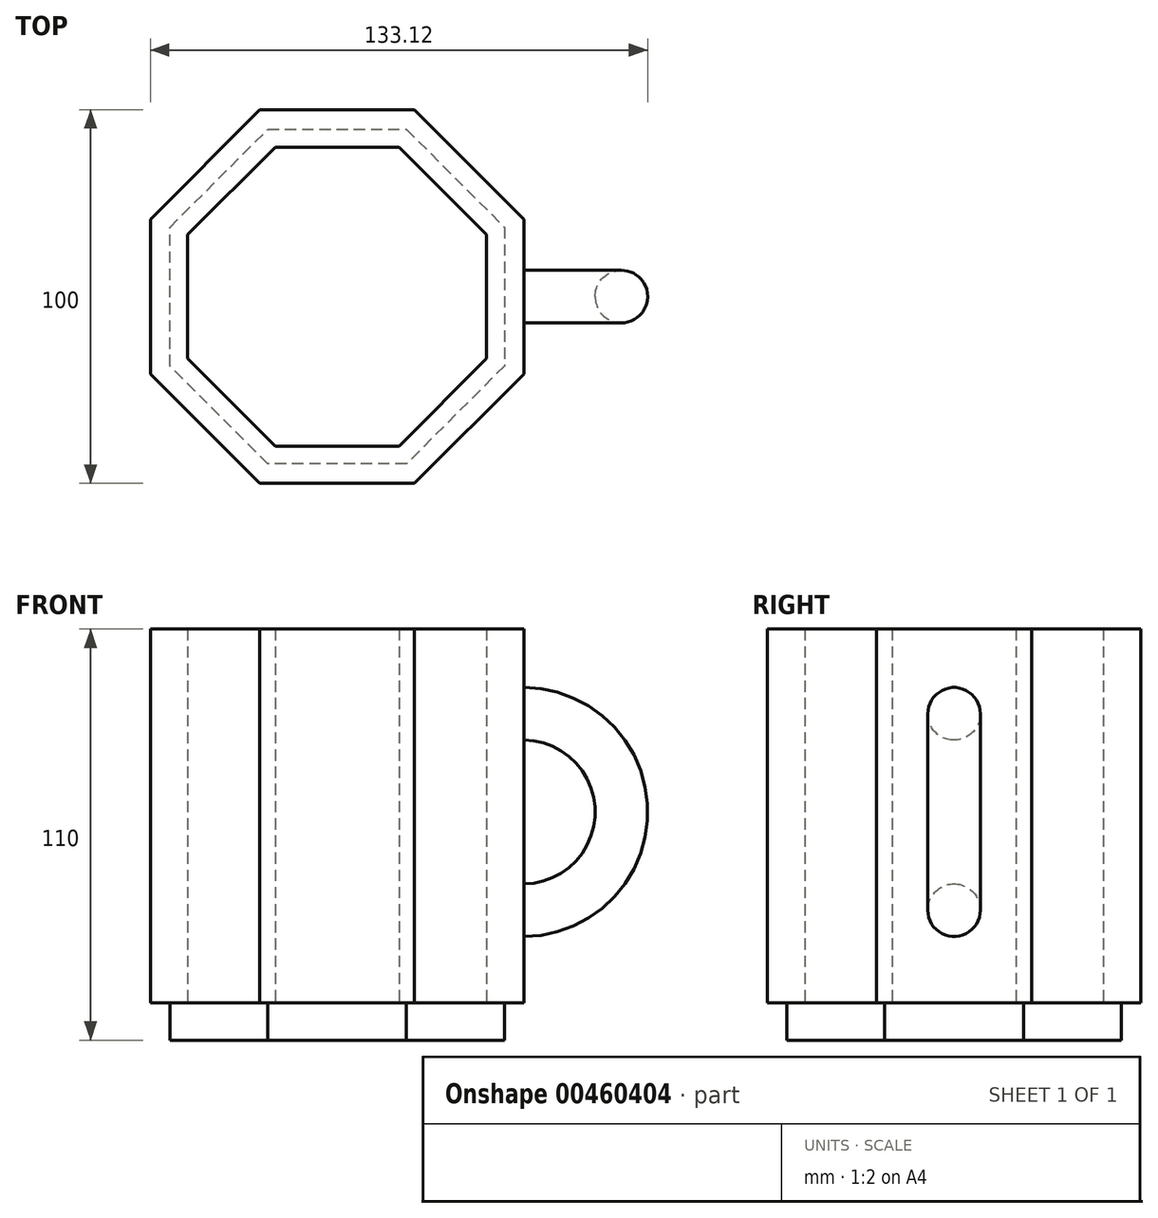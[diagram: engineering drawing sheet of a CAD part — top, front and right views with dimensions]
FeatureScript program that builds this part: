
annotation { "Feature Type Name" : "Feature", "Feature Type Description" : "" }
export const myFeature = defineFeature(function(context is Context, id is Id, definition is map)
    precondition{}
    {
        {
            var Q0;
            Q0=qCreatedBy(makeId("Top.planeOp"),FACE);
            var sketch = newSketch(context, id + "F0", { "sketchPlane" : qUnion([Q0])});
            skCircle(sketch, "E0.cCircle", {"center": v(0, 0) * mm, "radius": 40 * mm, "construction": true});
            skLineSegment(sketch, "E0.0", {"start": v(-16.57, 40) * mm, "end": v(16.57, 40) * mm});
            skLineSegment(sketch, "E0.1", {"start": v(16.57, 40) * mm, "end": v(40, 16.57) * mm});
            skLineSegment(sketch, "E0.2", {"start": v(40, 16.57) * mm, "end": v(40, -16.57) * mm});
            skLineSegment(sketch, "E0.3", {"start": v(40, -16.57) * mm, "end": v(16.57, -40) * mm});
            skLineSegment(sketch, "E0.4", {"start": v(16.57, -40) * mm, "end": v(-16.57, -40) * mm});
            skLineSegment(sketch, "E0.5", {"start": v(-16.57, -40) * mm, "end": v(-40, -16.57) * mm});
            skLineSegment(sketch, "E0.6", {"start": v(-40, -16.57) * mm, "end": v(-40, 16.57) * mm});
            skLineSegment(sketch, "E0.7", {"start": v(-40, 16.57) * mm, "end": v(-16.57, 40) * mm});
            skPoint(sketch, "E0.0.midPoint", {"position": v(0, 40) * mm});
            skCircle(sketch, "E1.cCircle", {"center": v(0, 0) * mm, "radius": 50 * mm, "construction": true});
            skLineSegment(sketch, "E1.0", {"start": v(-20.71, 50) * mm, "end": v(20.71, 50) * mm});
            skLineSegment(sketch, "E1.1", {"start": v(20.71, 50) * mm, "end": v(50, 20.71) * mm});
            skLineSegment(sketch, "E1.2", {"start": v(50, 20.71) * mm, "end": v(50, -20.71) * mm});
            skLineSegment(sketch, "E1.3", {"start": v(50, -20.71) * mm, "end": v(20.71, -50) * mm});
            skLineSegment(sketch, "E1.4", {"start": v(20.71, -50) * mm, "end": v(-20.71, -50) * mm});
            skLineSegment(sketch, "E1.5", {"start": v(-20.71, -50) * mm, "end": v(-50, -20.71) * mm});
            skLineSegment(sketch, "E1.6", {"start": v(-50, -20.71) * mm, "end": v(-50, 20.71) * mm});
            skLineSegment(sketch, "E1.7", {"start": v(-50, 20.71) * mm, "end": v(-20.71, 50) * mm});
            skPoint(sketch, "E1.0.midPoint", {"position": v(0, 50) * mm});
            skArc(sketch, "E2", {"start": v(49.14, -9.23) * mm, "mid": v(59.27, 0) * mm, "end": v(49.14, 9.23) * mm});
            skSolve(sketch);
        }
        {
            var Q0;
            Q0=makeQuery(id+"F0.imprint","IMPRINT",FACE,{"disambiguationData":[TD([[makeQuery(id+"F0.imprint","IMPRINT",EDGE,{"derivedFrom":sQuery(id+"F0.wireOp",EDGE,"E0.0")}),1.0]])]});
            extrude(context, id + "F1", {"entities" : qUnion([Q0]), "depth" : 100 * mm});
        }
        {
            var Q0;
            Q0=makeQuery(id+"F1.opExtrude","SWEPT_FACE",FACE,{"disambiguationData":[OSD([sQuery(id+"F0.wireOp",EDGE,"E1.2")])]});
            var sketch = newSketch(context, id + "F2", { "sketchPlane" : qUnion([Q0])});
            skCircle(sketch, "E3", {"center": v(0, 77.35) * mm, "radius": 7.04 * mm});
            skSolve(sketch);
        }
        {
            var Q0;
            Q0=qCreatedBy(makeId("Front.planeOp"),FACE);
            var sketch = newSketch(context, id + "F3", { "sketchPlane" : qUnion([Q0])});
            skLineSegment(sketch, "E4", {"start": v(49.8, 88.18) * mm, "end": v(49.8, 13.96) * mm, "construction": true});
            skArc(sketch, "E5", {"start": v(49.8, 24.17) * mm, "mid": v(76.69, 51.07) * mm, "end": v(49.8, 77.97) * mm});
            skSolve(sketch);
        }
        {
            var Q0;
            Q0=makeQuery(id+"F2.imprint","IMPRINT",FACE,{"disambiguationData":[TD([[makeQuery(id+"F2.imprint","IMPRINT",EDGE,{"derivedFrom":sQuery(id+"F2.wireOp",EDGE,"E3")}),1.0]])]});
            var Q1;
            Q1=sQuery(id+"F3.wireOp",EDGE,"E5");
            sweep(context, id + "F4", {"operationType" : NewBodyOperationType.ADD, "profiles" : qUnion([Q0]), "path" : qUnion([Q1])});
        }
        {
            var Q0;
            Q0=qCreatedBy(makeId("Top.planeOp"),FACE);
            var sketch = newSketch(context, id + "F5", { "sketchPlane" : qUnion([Q0])});
            skCircle(sketch, "E6.cCircle", {"center": v(0, 0) * mm, "radius": 44.78 * mm, "construction": true});
            skLineSegment(sketch, "E6.0", {"start": v(18.55, -44.78) * mm, "end": v(-18.55, -44.78) * mm});
            skLineSegment(sketch, "E6.1", {"start": v(-18.55, -44.78) * mm, "end": v(-44.78, -18.55) * mm});
            skLineSegment(sketch, "E6.2", {"start": v(-44.78, -18.55) * mm, "end": v(-44.78, 18.55) * mm});
            skLineSegment(sketch, "E6.3", {"start": v(-44.78, 18.55) * mm, "end": v(-18.55, 44.78) * mm});
            skLineSegment(sketch, "E6.4", {"start": v(-18.55, 44.78) * mm, "end": v(18.55, 44.78) * mm});
            skLineSegment(sketch, "E6.5", {"start": v(18.55, 44.78) * mm, "end": v(44.78, 18.55) * mm});
            skLineSegment(sketch, "E6.6", {"start": v(44.78, 18.55) * mm, "end": v(44.78, -18.55) * mm});
            skLineSegment(sketch, "E6.7", {"start": v(44.78, -18.55) * mm, "end": v(18.55, -44.78) * mm});
            skPoint(sketch, "E6.0.midPoint", {"position": v(0, -44.78) * mm});
            skSolve(sketch);
        }
        {
            var Q0;
            Q0=makeQuery(id+"F5.imprint","IMPRINT",FACE,{"disambiguationData":[TD([[makeQuery(id+"F5.imprint","IMPRINT",EDGE,{"derivedFrom":sQuery(id+"F5.wireOp",EDGE,"E6.0")}),-1.0]])]});
            extrude(context, id + "F6", {"entities" : qUnion([Q0]), "operationType" : NewBodyOperationType.ADD, "oppositeDirection" : true, "depth" : 10 * mm});
        }
    });
